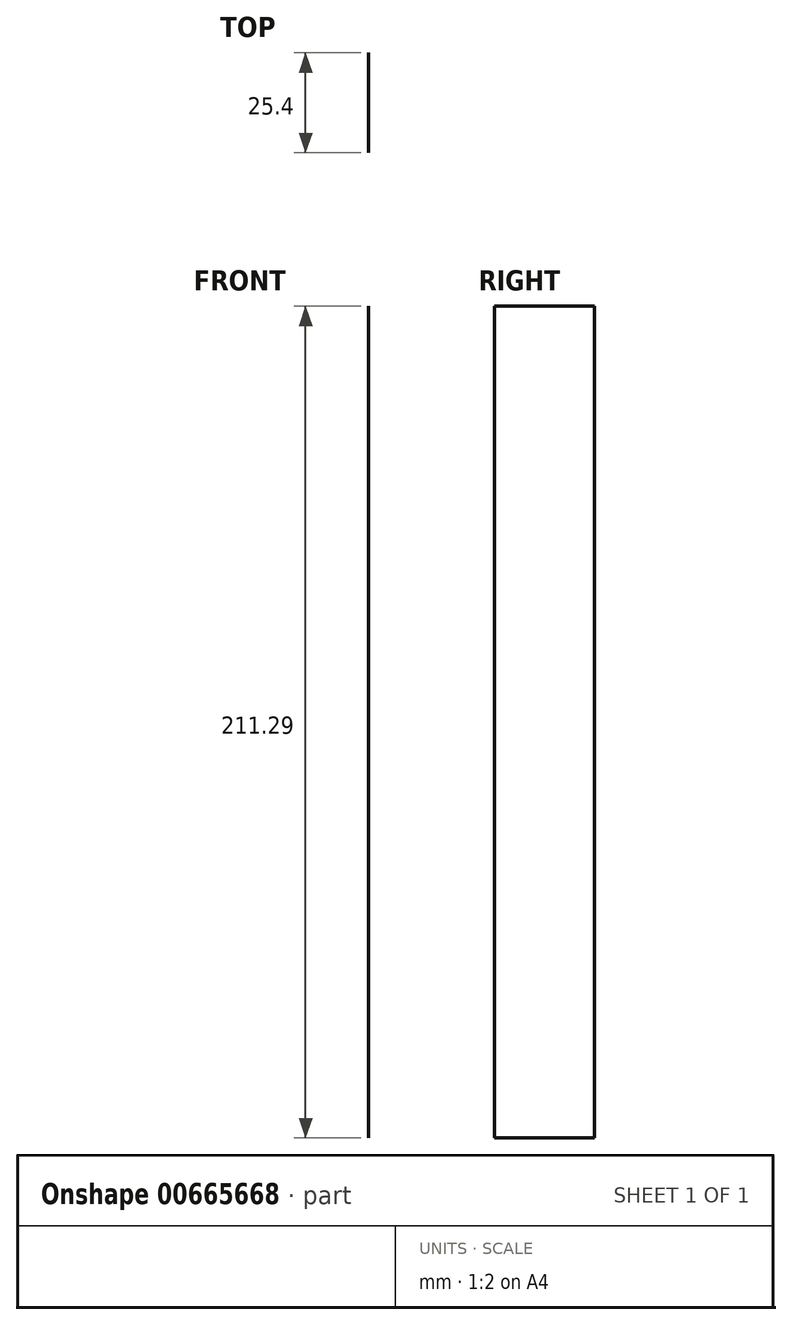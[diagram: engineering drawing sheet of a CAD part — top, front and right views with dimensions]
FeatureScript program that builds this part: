
annotation { "Feature Type Name" : "Feature", "Feature Type Description" : "" }
export const myFeature = defineFeature(function(context is Context, id is Id, definition is map)
    precondition{}
    {
        {
            var Q0;
            Q0=qCreatedBy(makeId("Front.planeOp"),FACE);
            var sketch = newSketch(context, id + "F0", { "sketchPlane" : qUnion([Q0])});
            skLineSegment(sketch, "E0.bottom", {"start": v(-72.53, -61.3) * mm, "end": v(83.54, -61.3) * mm});
            skLineSegment(sketch, "E0.top", {"start": v(-72.53, 149.99) * mm, "end": v(83.54, 149.99) * mm});
            skLineSegment(sketch, "E0.left", {"start": v(-72.53, -61.3) * mm, "end": v(-72.53, 149.99) * mm});
            skLineSegment(sketch, "E0.right", {"start": v(83.54, -61.3) * mm, "end": v(83.54, 149.99) * mm});
            skSolve(sketch);
        }
        {
            var Q0;
            Q0=sQuery(id+"F0.wireOp",EDGE,"E0.left");
            extrude(context, id + "F1", {"bodyType" : ToolBodyType.SURFACE, "surfaceEntities" : qUnion([Q0]), "depth" : 25.4 * mm, "offsetDistance" : 25.4 * mm});
        }
    });
